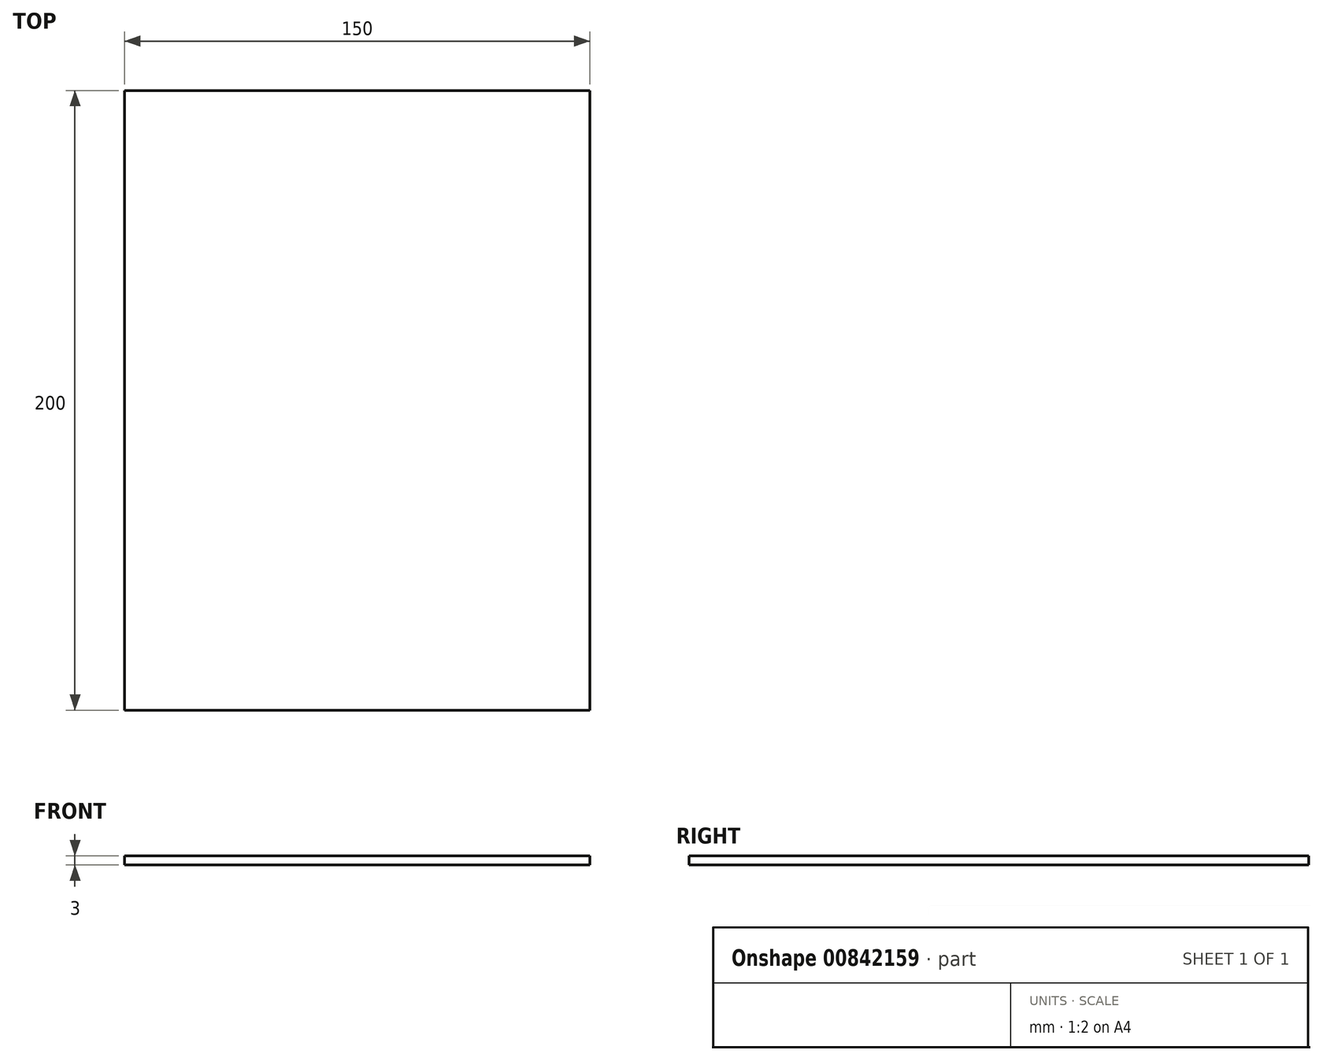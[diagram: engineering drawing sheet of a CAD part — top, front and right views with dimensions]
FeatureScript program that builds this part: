
annotation { "Feature Type Name" : "Feature", "Feature Type Description" : "" }
export const myFeature = defineFeature(function(context is Context, id is Id, definition is map)
    precondition{}
    {
        {
            var Q0;
            Q0=qCreatedBy(makeId("Top.planeOp"),FACE);
            var sketch = newSketch(context, id + "F0", { "sketchPlane" : qUnion([Q0])});
            skLineSegment(sketch, "E0.bottom", {"start": v(75, 100) * mm, "end": v(-75, 100) * mm});
            skLineSegment(sketch, "E0.top", {"start": v(75, -100) * mm, "end": v(-75, -100) * mm});
            skLineSegment(sketch, "E0.left", {"start": v(75, 100) * mm, "end": v(75, -100) * mm});
            skLineSegment(sketch, "E0.right", {"start": v(-75, 100) * mm, "end": v(-75, -100) * mm});
            skPoint(sketch, "E0.middle", {"position": v(0, 0) * mm});
            skSolve(sketch);
        }
        {
            var Q0;
            Q0=makeQuery(id+"F0.imprint","IMPRINT",FACE,{"disambiguationData":[TD([[makeQuery(id+"F0.imprint","IMPRINT",EDGE,{"derivedFrom":sQuery(id+"F0.wireOp",EDGE,"E0.bottom")}),1.0]])]});
            extrude(context, id + "F1", {"entities" : qUnion([Q0]), "depth" : 3 * mm, "offsetDistance" : 25 * mm});
        }
    });
